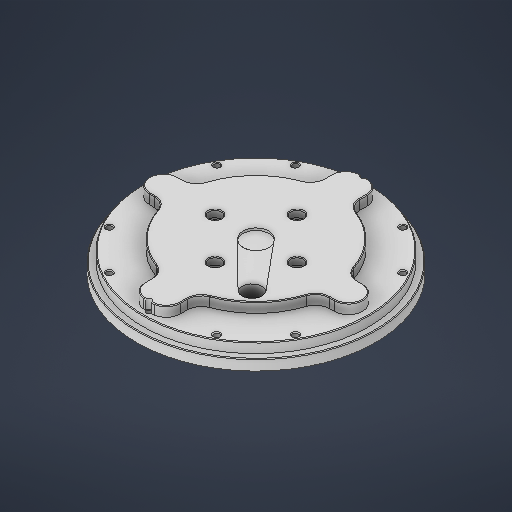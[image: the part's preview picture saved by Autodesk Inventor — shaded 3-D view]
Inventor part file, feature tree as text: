
AUTODESK INVENTOR PART (.ipt)
format: ipt  version: 2025 (Build 290162000, 162)  size: 523,776 bytes
history: native  units: in
note: dims shown in document units (in); Inventor stores cm internally (conversion verified against a paired STEP export)
features: sketch x14, extrude x9, hole x4, chamfer x3
ambient origin geometry x8: Origin, YZ Plane, XZ Plane, XY Plane, X Axis, Y Axis, Z Axis, Center Point
bodies: Solid1 (feature_tree)
feature tree (30):
  sketch  "Sketch1"  dims[d3=4.3307in d24=6.6535in]
  extrude  "Extrusion1"  Depth=6.6535in
  extrude  "Extrusion2"  Depth=5.9843in
  extrude  "Extrusion3"  Depth=4.3307in
  sketch  "Sketch2"  dims[d27=0.9843in d28=4.3307in]
  extrude  "Extrusion4"  Depth=0.3937in
  hole  "Hole1"  [1 undecoded]
  hole  "Hole2"  [1 undecoded]
  sketch  "Sketch4"  dims[d38=0.2953in d39=0.0in d40=2.2835in]
  extrude  "Extrusion5"  Depth=2.2835in
  extrude  "Extrusion6"  Depth=0.1969in
  hole  "Hole3"  [1 undecoded]
  chamfer  "Chamfer1"  Distance=0.7874in Angle=360.0deg
  chamfer  "Chamfer2"  Distance=0.1969in
  hole  "Hole5"  [1 undecoded]
  extrude  "Extrusion9"  Depth=0.0591in TaperAngle=0.0deg
  extrude  "Extrusion10"  Depth=0.0197in TaperAngle=0.0deg
  chamfer  "Chamfer4"  Distance=0.1969in
  extrude  "Extrusion11"  Depth=0.0197in TaperAngle=360.0deg
  sketch  "Sketch Circular Pattern1"  dims[d25=6.2992in d26=5.9843in]
  sketch  "Sketch3"  dims[d31=0.3937in d32=0.3937in]
  sketch  "Sketch Circular Pattern2"  dims[d29=0.7874in d30=0.3937in]
  sketch  "Sketch5"  dims[d41=0.3543in d42=0.1969in]
  sketch  "Sketch Circular Pattern3"  dims[d34=0.8465in d35=0.0in d36=0.5709in d37=0.0in]
  sketch  "Sketch7"  dims[d56=5.9843in]
  sketch  "Sketch Circular Pattern5"  dims[d43=1.5748in d45=360.0deg d47=0.1969in d48=0.0in]
  sketch  "Sketch9"  dims[d57=0.1378in d58=0.7874in d60=360.0deg]
  sketch  "Sketch Circular Pattern6"  dims[d49=0.2165in d50=0.7874in d51=0.1575in d52=0.0787in d53=90.0deg d54=0.315in d55=0.8108in]
  sketch  "Sketch10"  dims[d62=0.1276in d63=1.0025in d64=0.1575in d65=0.2756in d66=90.0deg d67=0.4646in d68=0.0in]
  sketch  "Sketch11"  dims[d69=3.2283in d70=0.1969in d71=0.7874in d72=0.0591in d73=0.0in d74=0.4724in d75=0.0in d76=0.1969in d77=4.7244in d79=360.0deg d81=0.1628in d82=0.7874in d83=0.1575in d84=0.0787in d85=90.0deg d86=0.3937in d87=0.8108in d88=0.0197in d89=0.0787in d90=45.0deg d91=0.0197in d92=0.0787in d93=45.0deg d107=3.7402in d108=0.1969in d109=6.2992in d111=360.0deg d113=0.1969in d114=0.7874in d115=0.748in d116=0.3543in d117=90.0deg d118=0.7874in d119=0.8108in d139=0.7185in d140=3.1496in d141=0.7185in d142=3.1496in d144=360.0deg d146=0.0591in d147=0.0in d151=0.5512in d152=1.7717in d153=0.0in d154=0.0in d155=0.0197in d156=0.0787in d157=45.0deg d158=0.5512in d159=1.7717in d160=0.0394in d161=0.0in d162=0.1969in d137=0.0197in d138=0.0344in]
note: 4 required parameter values undecoded (feature->parameter linkage not recoverable at this tier; creation-order binding heuristic only, values carry confidence <= 0.55)
